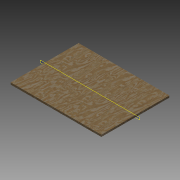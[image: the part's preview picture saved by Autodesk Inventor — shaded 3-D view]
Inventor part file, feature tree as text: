
AUTODESK INVENTOR PART (.ipt)
format: ipt  version: 2016 (Build 200138000, 138)  size: 87,552 bytes
history: native  units: in
note: dims shown in document units (in); Inventor stores cm internally (conversion verified against a paired STEP export)
features: extrude x1, plane x1, sketch x1
ambient origin geometry x8: Origin, YZ Plane, XZ Plane, XY Plane, X Axis, Y Axis, Z Axis, Center Point
bodies: Solid1 (feature_tree)
feature tree (3):
  extrude  "Extrusion1"  Depth=48.0in
  plane  "Work Plane1"
  sketch  "Sketch1"  dims[d0=36.0in d1=48.0in d2=1.0in d3=0.0in]
